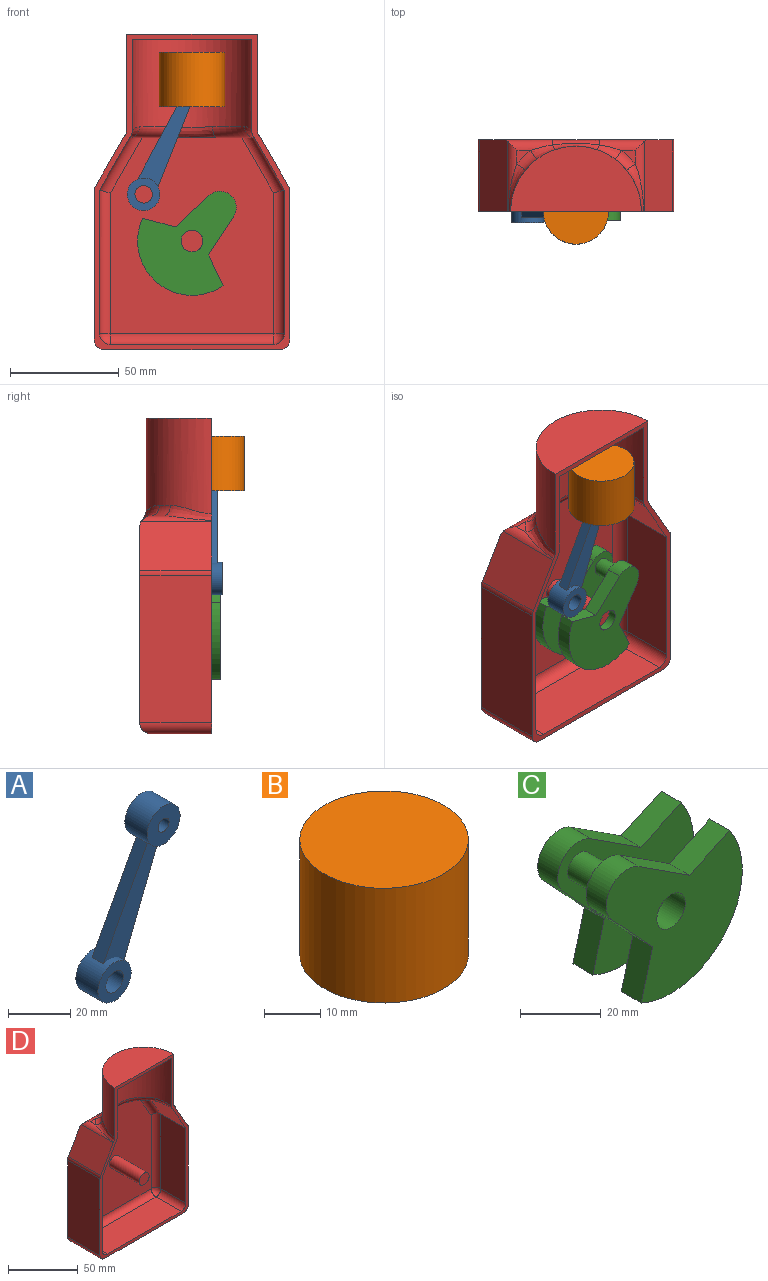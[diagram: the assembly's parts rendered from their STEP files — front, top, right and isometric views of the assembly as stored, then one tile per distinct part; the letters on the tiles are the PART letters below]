
ASSEMBLY  parts=4 mates=4
PART A: 12 faces, bbox 37.2x10x65.3 mm
  f0: cylinder r=4mm len=10mm, axis (0,1,0), area 251.3mm2, adj f2,f3
  f1: cylinder r=7.5mm len=15mm, axis (0,1,0), area 416.5mm2, adj f2,f3,f8,f9,f10,f11
  f2: plane 15x15mm, normal (0,-1,0), area 126.4mm2, adj f0,f1
  f3: plane 15x15mm, normal (0,1,0), area 126.4mm2, adj f0,f1
  f4: cylinder r=2.5mm len=10mm, axis (0,1,0), area 157.1mm2, adj f6,f7
  f5: cylinder r=7.5mm len=15mm, axis (0,1,0), area 445.8mm2, adj f6,f7,f8,f9,f10,f11
  f6: plane 15x15mm, normal (0,-1,0), area 157.1mm2, adj f4,f5
  f7: plane 15x15mm, normal (0,1,0), area 157.1mm2, adj f4,f5
  f8: plane 39.37x15.55mm, normal (0.93,0,-0.37), area 211.6mm2, adj f1,f5,f10,f11
  f9: plane 37.48x20.18mm, normal (-0.88,0,0.47), area 212.8mm2, adj f1,f5,f10,f11
  f10: plane 41.03x24.9mm, normal (0,-1,0), area 302.2mm2, adj f1,f5,f8,f9
  f11: plane 41.03x24.9mm, normal (0,1,0), area 302.2mm2, adj f1,f5,f8,f9
PART B: 17 faces, bbox 30x30x25 mm
  f0: cylinder r=5mm len=10mm, axis (0,1,0), area 101.5mm2, adj f1,f7,f8,f11
  f1: cylinder r=12mm len=24mm, axis (0,0,1), area 1330.9mm2, adj f0,f2,f3,f6,f7,f8,f9
  f2: plane 21.82x7mm, normal (0,0,-1), area 109.8mm2, adj f1,f7
  f3: plane 30x30mm, normal (0,0,-1), area 254.5mm2, adj f1,f4
  f4: cylinder r=15mm len=30mm, axis (0,0,1), area 2356.2mm2, adj f3,f5
  f5: plane 30x30mm, normal (0,0,1), area 706.9mm2, adj f4
  f6: plane 21.82x7mm, normal (0,0,-1), area 109.8mm2, adj f1,f8
  f7: plane 21.82x12mm, normal (-1,0,0), area 181.8mm2, adj f0,f1,f2,f9,f10,f11,f12
  f8: plane 21.82x12mm, normal (1,0,0), area 181.8mm2, adj f0,f1,f6,f9,f10,f11,f12
  f9: cylinder r=5mm len=10mm, axis (0,1,0), area 101.5mm2, adj f1,f7,f8,f12
  f10: plane 10x10mm, normal (0,0,-1), area 100mm2, adj f7,f8,f11,f12
  f11: plane 13x10mm, normal (0,-1,0), area 99.6mm2, adj f0,f7,f8,f10,f15
  f12: plane 13x10mm, normal (0,1,0), area 99.6mm2, adj f7,f8,f9,f10,f14
  f13: cylinder r=12mm len=5mm, axis (0,0,1), area 19.7mm2, adj f14
  f14: cylinder r=2.5mm len=7mm, axis (0,1,0), area 107.9mm2, adj f12,f13
  f15: cylinder r=2.5mm len=7mm, axis (0,1,0), area 107.9mm2, adj f11,f16
  f16: cylinder r=12mm len=5mm, axis (0,0,1), area 19.7mm2, adj f15
PART C: 19 faces, bbox 47.8x24x45.4 mm
  f0: plane 14.12x7mm, normal (-0.42,0,0.91), area 109mm2, adj f1,f6,f7,f10
  f1: plane 17.66x11.48mm, normal (0.55,0,0.84), area 147.5mm2, adj f0,f2,f7,f10
  f2: cylinder r=7.5mm len=12.62mm, axis (0,1,0), area 152.2mm2, adj f1,f3,f7,f10
  f3: plane 15.4x14.38mm, normal (-0.73,0,-0.68), area 147.5mm2, adj f2,f4,f7,f10
  f4: plane 15.05x7mm, normal (-0.97,0,0.26), area 109mm2, adj f3,f6,f7,f10
  f5: cylinder r=5mm len=10mm, axis (0,1,0), area 219.9mm2, adj f7,f10
  f6: cylinder r=25mm len=39.24mm, axis (0,1,0), area 456.5mm2, adj f0,f4,f7,f10
  f7: plane 47.82x45.36mm, normal (0,-1,0), area 1242mm2, adj f0,f1,f2,f3,f4,f5,f6
  f8: cylinder r=4mm len=10mm, axis (0,-1,0), area 251.3mm2, adj f9,f10
  f9: plane 47.82x45.36mm, normal (0,-1,0), area 1191.7mm2, adj f8,f11,f13,f14,f15,f16,f17,f18
  f10: plane 47.82x45.36mm, normal (0,1,0), area 1191.7mm2, adj f0,f1,f2,f3,f4,f5,f6,f8
  f11: cylinder r=5mm len=10mm, axis (0,1,0), area 219.9mm2, adj f9,f12
  f12: plane 47.82x45.36mm, normal (0,1,0), area 1242mm2, adj f11,f13,f14,f15,f16,f17,f18
  f13: cylinder r=25mm len=39.24mm, axis (0,1,0), area 456.5mm2, adj f9,f12,f14,f18
  f14: plane 15.05x7mm, normal (-0.97,0,0.26), area 109mm2, adj f9,f12,f13,f15
  f15: plane 15.4x14.38mm, normal (-0.73,0,-0.68), area 147.5mm2, adj f9,f12,f14,f16
  f16: cylinder r=7.5mm len=12.62mm, axis (0,1,0), area 152.2mm2, adj f9,f12,f15,f17
  f17: plane 17.66x11.48mm, normal (0.55,0,0.84), area 147.5mm2, adj f9,f12,f16,f18
  f18: plane 14.12x7mm, normal (-0.42,0,0.91), area 109mm2, adj f9,f12,f13,f17
PART D: 54 faces, bbox 91.2x35.8x146.2 mm
  f0: plane 6.11x5.87mm, normal (0,0,1), area 16.5mm2, adj f35,f36,f46
  f1: plane 18.55x16.2mm, normal (0,0,-1), area 91.6mm2, adj f19,f20,f21,f31
  f2: cylinder r=30mm len=60mm, axis (0,0,-1), area 3892.7mm2, adj f3,f4,f45,f46,f47,f48,f49,f50
  f3: plane 60x30mm, normal (0,0,1), area 1413.7mm2, adj f2,f4
  f4: plane 145.01x90.01mm, normal (0,-1,0), area 1094.6mm2, adj f2,f3,f6,f7,f8,f9,f10,f12
  f5: plane 6.11x5.87mm, normal (0,0,1), area 16.5mm2, adj f38,f39,f50
  f6: plane 33.05x22.37mm, normal (-0.87,0,0.5), area 849.9mm2, adj f4,f11,f38,f39,f40
  f7: plane 67.68x33mm, normal (-1,0,0), area 2233.4mm2, adj f4,f11,f40,f43
  f8: plane 80x28mm, normal (0,0,-1), area 2240mm2, adj f4,f41,f42,f43
  f9: plane 67.68x33mm, normal (1,0,0), area 2233.4mm2, adj f4,f11,f41,f44
  f10: plane 33.05x22.37mm, normal (0.87,0,0.5), area 849.9mm2, adj f4,f11,f35,f36,f44
  f11: plane 90.42x90mm, normal (0,1,0), area 7850.2mm2, adj f6,f7,f9,f10,f36,f37,f38,f40
  f12: cylinder r=27.5mm len=55mm, axis (0,0,-1), area 3482.1mm2, adj f4,f13,f30,f31,f32,f33,f34
  f13: plane 55x27.5mm, normal (0,0,-1), area 1187.9mm2, adj f4,f12
  f14: plane 18.55x16.2mm, normal (0,0,-1), area 91.6mm2, adj f15,f20,f24,f33
  f15: plane 25.97x24.62mm, normal (0.87,0,-0.5), area 711.1mm2, adj f4,f14,f16,f24,f34
  f16: plane 65.85x25.5mm, normal (1,0,0), area 1679.2mm2, adj f4,f15,f26,f29
  f17: plane 75x25.5mm, normal (0,0,1), area 1912.5mm2, adj f4,f23,f27,f29
  f18: plane 65.85x25.5mm, normal (-1,0,0), area 1679.2mm2, adj f4,f19,f22,f23
  f19: plane 25.97x24.62mm, normal (-0.87,0,-0.5), area 711.1mm2, adj f1,f4,f18,f21,f30
  f20: plane 90.19x75.19mm, normal (0,-1,0), area 6296.3mm2, adj f1,f14,f21,f22,f24,f26,f27,f32
  f21: cylinder r=5mm len=29.15mm, axis (-0.5,0,0.87), area 225.1mm2, adj f1,f19,f20,f22
  f22: cylinder r=5mm len=65.85mm, axis (0,0,1), area 511.9mm2, adj f18,f20,f21,f25
  f23: cylinder r=5mm len=25.5mm, axis (0,-1,0), area 200.3mm2, adj f4,f17,f18,f25
  f24: cylinder r=5mm len=29.15mm, axis (-0.5,0,-0.87), area 225.1mm2, adj f14,f15,f20,f26
  f25: sphere r=5mm, area 25mm2, adj f22,f23,f27
  f26: cylinder r=5mm len=65.85mm, axis (0,0,-1), area 511.9mm2, adj f16,f20,f24,f28
  f27: cylinder r=5mm len=75mm, axis (1,0,0), area 589mm2, adj f17,f20,f25,f28
  f28: sphere r=5mm, area 53.5mm2, adj f26,f27,f29
  f29: cylinder r=5mm len=25.5mm, axis (0,1,0), area 200.3mm2, adj f4,f16,f17,f28
  f30: bspline ~17.75x5.33mm, area 70.1mm2, adj f4,f12,f19,f31
  f31: torus R=32.5mm, axis (0,0,-1), area 165.9mm2, adj f1,f12,f30,f32
  f32: bspline ~23.84x5.32mm, area 131.8mm2, adj f12,f20,f31,f33
  f33: torus R=32.5mm, axis (0,0,-1), area 165.9mm2, adj f12,f14,f32,f34
  f34: bspline ~17.75x5.33mm, area 70.1mm2, adj f4,f12,f15,f33
  f35: cylinder r=5mm len=32.33mm, axis (0,-1,0), area 92.5mm2, adj f0,f4,f10,f36,f45
  f36: cylinder r=5mm len=22.12mm, axis (1,0,0), area 138.6mm2, adj f0,f10,f11,f35,f37,f47
  f37: bspline ~25.2x5.78mm, area 89.9mm2, adj f11,f36,f38,f48
  f38: cylinder r=5mm len=22.12mm, axis (1,0,0), area 138.6mm2, adj f5,f6,f11,f37,f39,f49
  f39: cylinder r=5mm len=32.33mm, axis (0,1,0), area 92.5mm2, adj f4,f5,f6,f38,f51
  f40: cylinder r=5mm len=33mm, axis (0,-1,0), area 86.4mm2, adj f4,f6,f7,f11
  f41: cylinder r=5mm len=33mm, axis (0,1,0), area 239.5mm2, adj f4,f8,f9,f42
  f42: cylinder r=5mm len=90mm, axis (-1,0,0), area 667.6mm2, adj f8,f11,f41,f43
  f43: cylinder r=5mm len=33mm, axis (0,-1,0), area 239.5mm2, adj f4,f7,f8,f42
  f44: cylinder r=5mm len=33mm, axis (0,-1,0), area 86.4mm2, adj f4,f9,f10,f11
  f45: bspline ~24.24x8.76mm, area 107.8mm2, adj f2,f4,f35,f46
  f46: torus R=35mm, axis (0,0,-1), area 60.6mm2, adj f0,f2,f45,f47
  f47: bspline ~15.05x8.61mm, area 64.1mm2, adj f2,f36,f46,f48
  f48: bspline ~23.35x4.66mm, area 88.1mm2, adj f2,f37,f47,f49
  f49: bspline ~15.05x8.61mm, area 64.1mm2, adj f2,f38,f48,f50
  f50: torus R=35mm, axis (0,0,-1), area 60.6mm2, adj f2,f5,f49,f51
  f51: bspline ~24.24x8.76mm, area 107.8mm2, adj f2,f4,f39,f50
  f52: cylinder r=5mm len=30.45mm, axis (0,1,0), area 956.6mm2, adj f20,f53
  f53: plane 10x10mm, normal (0,-1,0), area 78.5mm2, adj f52
PLACE A rot(axis=(0,1,0),0deg) t=(2.24,9.13,119.62)mm
PLACE B t=(2.24,9.13,115.98)mm
PLACE C rot(axis=(0,1,0),90deg) t=(2.24,17.13,109.92)mm
PLACE D t=(2.24,9.13,59.92)mm fixed
MATE revolute A.f0 <-> C.f2  axis (0,1,0) through (-19.96,9.13,131.34)mm
MATE slider B.f1 <-> D.f2  axis (0,0,1) through (2.24,9.13,196.66)mm
MATE revolute D.f52 <-> C.f5  axis (0,1,0) through (2.24,9.18,109.92)mm
MATE revolute A.f4 <-> B.f0  axis (0,1,0) through (2.24,14.13,181.66)mm
